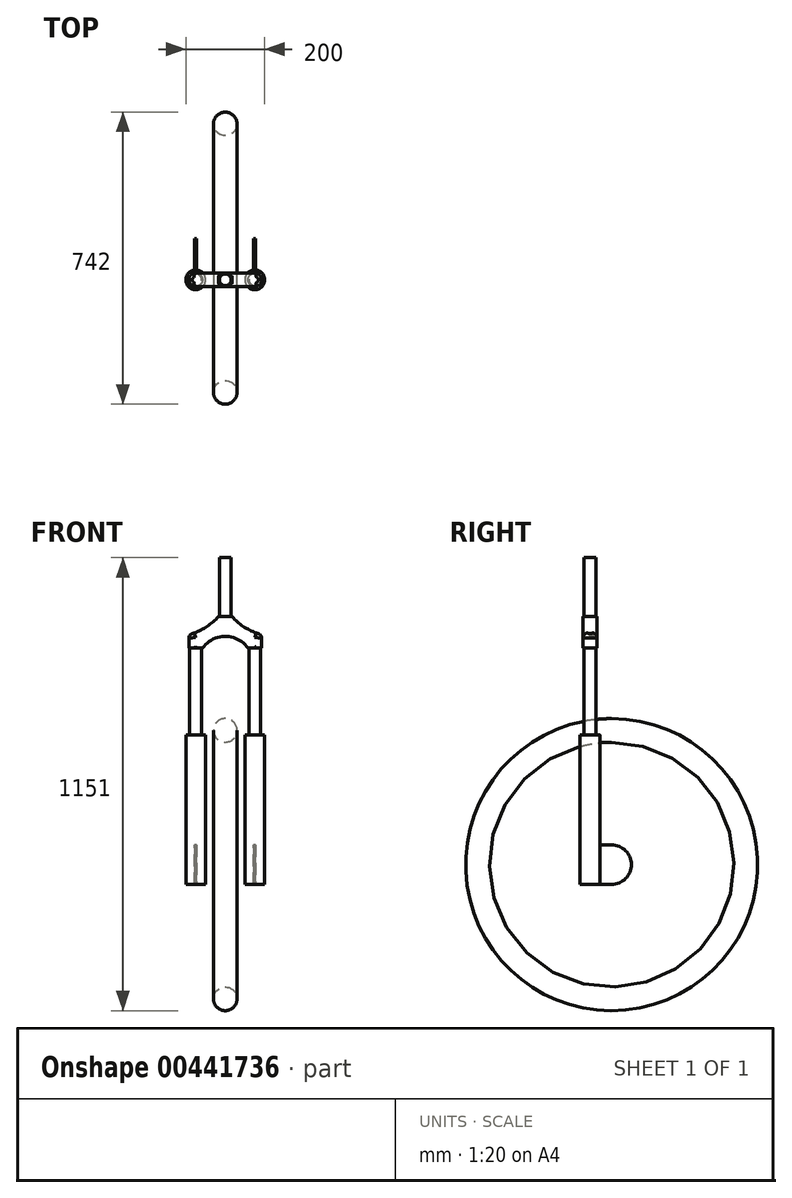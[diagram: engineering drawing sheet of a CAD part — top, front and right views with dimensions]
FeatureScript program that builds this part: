
annotation { "Feature Type Name" : "Feature", "Feature Type Description" : "" }
export const myFeature = defineFeature(function(context is Context, id is Id, definition is map)
    precondition{}
    {
        {
            var Q0;
            Q0=qCreatedBy(makeId("Front.planeOp"),FACE);
            var sketch = newSketch(context, id + "F0", { "sketchPlane" : qUnion([Q0])});
            skCircle(sketch, "E0", {"center": v(0, 341) * mm, "radius": 30 * mm});
            skLineSegment(sketch, "E1", {"start": v(-90.17, 0) * mm, "end": v(113.83, 0) * mm, "construction": true});
            skSolve(sketch);
        }
        {
            var Q0;
            Q0=makeQuery(id+"F0.imprint","IMPRINT",FACE,{"disambiguationData":[TD([[makeQuery(id+"F0.imprint","IMPRINT",EDGE,{"derivedFrom":sQuery(id+"F0.wireOp",EDGE,"E0")}),1.0]])]});
            var Q1;
            Q1=sQuery(id+"F0.wireOp",EDGE,"E1");
            revolve(context, id + "F1", {"entities" : qUnion([Q0]), "axis" : qUnion([Q1]), "revolveType" : RevolveType.FULL});
        }
        {
            var Q0;
            Q0=qCreatedBy(makeId("Top.planeOp"),FACE);
            var sketch = newSketch(context, id + "F2", { "sketchPlane" : qUnion([Q0])});
            skCircle(sketch, "E2", {"center": v(-75, -55) * mm, "radius": 25 * mm});
            skLineSegment(sketch, "E3", {"start": v(0, 0) * mm, "end": v(0, -163.23) * mm, "construction": true});
            skLineSegment(sketch, "E4", {"start": v(0, 0) * mm, "end": v(-223.49, 0) * mm, "construction": true});
            skLineSegment(sketch, "E5", {"start": v(-75, -55) * mm, "end": v(82.16, -55) * mm, "construction": true});
            skSolve(sketch);
        }
        {
            var Q0;
            Q0 = qSketchRegion(id + "F2", true);
            extrude(context, id + "F3", {"entities" : qUnion([Q0]), "depth" : 330 * mm, "hasSecondDirection" : true, "secondDirectionOppositeDirection" : true, "secondDirectionDepth" : 50 * mm});
        }
        {
            var Q0;
            Q0=sQuery(id+"F2.wireOp",VERTEX,"E2.center");
            var Q1;
            Q1=sQuery(id+"F2.wireOp",EDGE,"E5");
            cPlane(context, id + "F4", {"entities" : qUnion([Q0, Q1]), "cplaneType" : CPlaneType.LINE_POINT, "offset" : 25 * mm, "width" : 150 * mm, "height" : 150 * mm});
        }
        {
            var Q0;
            Q0=qCreatedBy(id+"F4.planeOp",FACE);
            var sketch = newSketch(context, id + "F5", { "sketchPlane" : qUnion([Q0])});
            skPoint(sketch, "E6.0", {"position": v(0, 0) * mm});
            skCircle(sketch, "E7", {"center": v(0, 0) * mm, "radius": 50 * mm});
            skLineSegment(sketch, "E8", {"start": v(0, 50) * mm, "end": v(-55, 50) * mm});
            skLineSegment(sketch, "E9", {"start": v(-55, 50) * mm, "end": v(-55, -50) * mm});
            skLineSegment(sketch, "E10", {"start": v(-55, -50) * mm, "end": v(0, -50) * mm});
            skSolve(sketch);
        }
        {
            var Q0;
            Q0 = qSketchRegion(id + "F5", true);
            extrude(context, id + "F6", {"entities" : qUnion([Q0]), "operationType" : NewBodyOperationType.ADD, "endBound" : BoundingType.SYMMETRIC, "depth" : 5 * mm});
        }
        {
            var Q0;
            Q0=makeQuery(id+"F3.opExtrude","SWEPT_BODY",BODY,{"disambiguationData":[OSD([sQuery(id+"F2.wireOp",EDGE,"E2")])]});
            var Q1;
            Q1=qCreatedBy(makeId("Right.planeOp"),FACE);
            mirror(context, id + "F7", {"entities" : qUnion([Q0]), "mirrorPlane" : qUnion([Q1])});
        }
        {
            var Q0;
            Q0=qCreatedBy(makeId("Front.planeOp"),FACE);
            var Q1;
            Q1=sQuery(id+"F2.wireOp",VERTEX,"E2.center");
            cPlane(context, id + "F8", {"entities" : qUnion([Q0, Q1]), "cplaneType" : CPlaneType.PLANE_POINT, "offset" : 25 * mm, "width" : 150 * mm, "height" : 150 * mm});
        }
        {
            var Q0;
            Q0=qCreatedBy(id+"F8.planeOp",FACE);
            var sketch = newSketch(context, id + "F9", { "sketchPlane" : qUnion([Q0])});
            skLineSegment(sketch, "E11", {"start": v(0, 528.19) * mm, "end": v(0, 197.14) * mm, "construction": true});
            skLineSegment(sketch, "E12", {"start": v(0, 630) * mm, "end": v(-17.5, 630) * mm});
            skArc(sketch, "E13", {"start": v(-92.5, 584.59) * mm, "mid": v(-51.6, 601.7) * mm, "end": v(-17.5, 630) * mm});
            skLineSegment(sketch, "E14", {"start": v(-92.5, 584.59) * mm, "end": v(-92.5, 550) * mm});
            skLineSegment(sketch, "E15", {"start": v(-92.5, 550) * mm, "end": v(-57.5, 550) * mm});
            skArc(sketch, "E16", {"start": v(0, 580) * mm, "mid": v(-32.43, 572.05) * mm, "end": v(-57.5, 550) * mm});
            skLineSegment(sketch, "E17", {"start": v(0, 580) * mm, "end": v(42.3, 580) * mm, "construction": true});
            skLineSegment(sketch, "E18", {"start": v(-75, 330) * mm, "end": v(-75, 550) * mm, "construction": true});
            skLineSegment(sketch, "E19.0", {"start": v(-100, 330) * mm, "end": v(-50, 330) * mm, "construction": true});
            skLineSegment(sketch, "E20.MirrorCS", {"start": v(92.5, 584.59) * mm, "end": v(92.5, 550) * mm});
            skLineSegment(sketch, "E21.MirrorCS", {"start": v(0, 630) * mm, "end": v(17.5, 630) * mm});
            skLineSegment(sketch, "E22.MirrorCS", {"start": v(92.5, 550) * mm, "end": v(57.5, 550) * mm});
            skArc(sketch, "E23.MirrorCS", {"start": v(0, 580) * mm, "mid": v(32.43, 572.05) * mm, "end": v(57.5, 550) * mm});
            skArc(sketch, "E24.MirrorCS", {"start": v(92.5, 584.59) * mm, "mid": v(51.6, 601.7) * mm, "end": v(17.5, 630) * mm});
            skSolve(sketch);
        }
        {
            var Q0;
            Q0 = qSketchRegion(id + "F9", true);
            extrude(context, id + "F10", {"entities" : qUnion([Q0]), "endBound" : BoundingType.SYMMETRIC, "depth" : 35 * mm});
        }
        {
            var Q0;
            Q0=makeQuery(id+"F10.opExtrude","CAP_EDGE",EDGE,{"disambiguationData":[OSD([sQuery(id+"F9.wireOp",EDGE,"E20.MirrorCS")])],"isStart":false});
            var Q1;
            Q1=makeQuery(id+"F10.opExtrude","CAP_EDGE",EDGE,{"disambiguationData":[OSD([sQuery(id+"F9.wireOp",EDGE,"E20.MirrorCS")])],"isStart":true});
            var Q2;
            Q2=makeQuery(id+"F10.opExtrude","CAP_EDGE",EDGE,{"disambiguationData":[OSD([sQuery(id+"F9.wireOp",EDGE,"E14")])],"isStart":false});
            var Q3;
            Q3=makeQuery(id+"F10.opExtrude","CAP_EDGE",EDGE,{"disambiguationData":[OSD([sQuery(id+"F9.wireOp",EDGE,"E14")])],"isStart":true});
            var Q4;
            Q4=makeQuery(id+"F10.opExtrude","CAP_EDGE",EDGE,{"disambiguationData":[OSD([sQuery(id+"F9.wireOp",EDGE,"E16"),sQuery(id+"F9.wireOp",EDGE,"E23.MirrorCS")])],"isStart":true});
            var Q5;
            Q5=makeQuery(id+"F10.opExtrude","CAP_EDGE",EDGE,{"disambiguationData":[OSD([sQuery(id+"F9.wireOp",EDGE,"E16"),sQuery(id+"F9.wireOp",EDGE,"E23.MirrorCS")])],"isStart":false});
            fillet(context, id + "F11", {"entities" : qUnion([Q0, Q1, Q2, Q3, Q4, Q5]), "radius" : 17.5 * mm, "tangentPropagation" : true, "allowEdgeOverflow" : false});
        }
        {
            var Q0;
            Q0=makeQuery(id+"F10.opExtrude","CAP_EDGE",EDGE,{"disambiguationData":[OSD([sQuery(id+"F9.wireOp",EDGE,"E13")])],"isStart":false});
            var Q1;
            Q1=makeQuery(id+"F10.opExtrude","CAP_EDGE",EDGE,{"disambiguationData":[OSD([sQuery(id+"F9.wireOp",EDGE,"E24.MirrorCS")])],"isStart":false});
            fillet(context, id + "F12", {"entities" : qUnion([Q0, Q1]), "radius" : 12 * mm, "tangentPropagation" : true, "allowEdgeOverflow" : false});
        }
        {
            var Q0;
            Q0=makeQuery(id+"F10.opExtrude","SWEPT_FACE",FACE,{"disambiguationData":[OSD([sQuery(id+"F9.wireOp",EDGE,"E12"),sQuery(id+"F9.wireOp",EDGE,"E21.MirrorCS")])]});
            var sketch = newSketch(context, id + "F13", { "sketchPlane" : qUnion([Q0])});
            skLineSegment(sketch, "E25", {"start": v(0, -87.89) * mm, "end": v(0, -15.82) * mm, "construction": true});
            skCircle(sketch, "E26", {"center": v(0, -55) * mm, "radius": 15 * mm});
            skSolve(sketch);
        }
        {
            var Q0;
            Q0 = qSketchRegion(id + "F13", true);
            extrude(context, id + "F14", {"entities" : qUnion([Q0]), "operationType" : NewBodyOperationType.ADD, "depth" : 150 * mm});
        }
        {
            var Q0;
            Q0=makeQuery(id+"F10.opExtrude","SWEPT_FACE",FACE,{"disambiguationData":[OSD([sQuery(id+"F9.wireOp",EDGE,"E15")])]});
            var sketch = newSketch(context, id + "F15", { "sketchPlane" : qUnion([Q0])});
            skCircle(sketch, "E27", {"center": v(-75, 55) * mm, "radius": 15 * mm});
            skLineSegment(sketch, "E28", {"start": v(0, 103.32) * mm, "end": v(0, 0) * mm, "construction": true});
            skCircle(sketch, "E29.MirrorC", {"center": v(75, 55) * mm, "radius": 15 * mm});
            skSolve(sketch);
        }
        {
            var Q0;
            Q0 = qSketchRegion(id + "F15", true);
            var Q1;
            Q1=makeQuery(id+"F7.opPattern","COPY",FACE,{"derivedFrom":makeQuery(id+"F3.opExtrude","CAP_FACE",FACE,{"disambiguationData":[OSD([sQuery(id+"F2.wireOp",EDGE,"E2")])],"isStart":false}),"instanceName":"1"});
            extrude(context, id + "F16", {"entities" : qUnion([Q0]), "operationType" : NewBodyOperationType.ADD, "endBoundEntityFace" : qUnion([Q1]), "depth" : 230 * mm});
        }
    });
